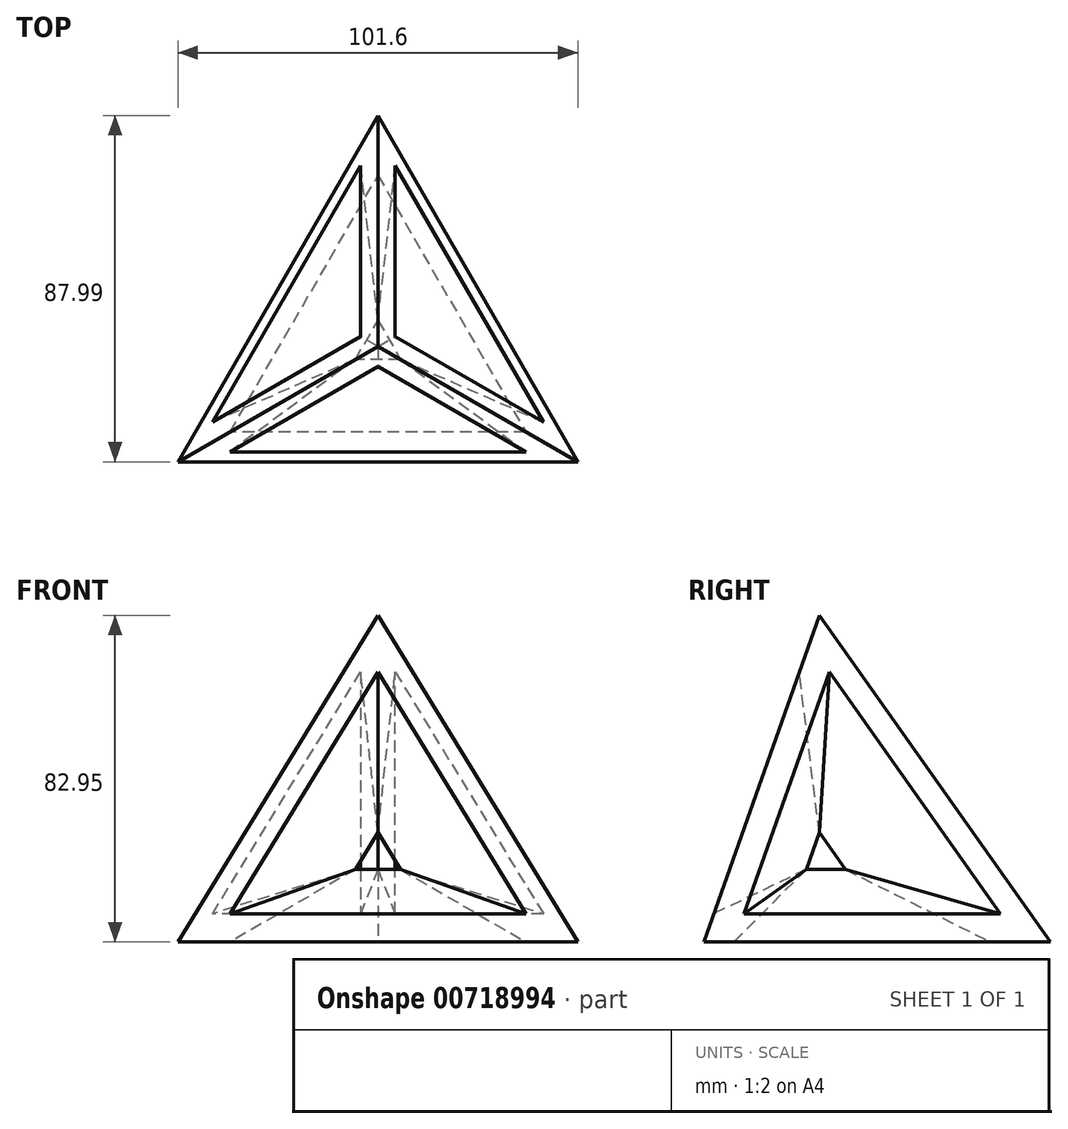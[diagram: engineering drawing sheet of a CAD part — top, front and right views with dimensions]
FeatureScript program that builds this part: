
annotation { "Feature Type Name" : "Feature", "Feature Type Description" : "" }
export const myFeature = defineFeature(function(context is Context, id is Id, definition is map)
    precondition{}
    {
        {
            var Q0;
            Q0=qCreatedBy(makeId("Top.planeOp"),FACE);
            var sketch = newSketch(context, id + "F0", { "sketchPlane" : qUnion([Q0])});
            skLineSegment(sketch, "E0", {"start": v(0, 87.99) * mm, "end": v(-50.8, 0) * mm});
            skLineSegment(sketch, "E1", {"start": v(-50.8, 0) * mm, "end": v(50.8, 0) * mm});
            skLineSegment(sketch, "E2", {"start": v(50.8, 0) * mm, "end": v(0, 87.99) * mm});
            skSolve(sketch);
        }
        {
            var Q0;
            Q0 = qSketchRegion(id + "F0", true);
            extrude(context, id + "F1", {"entities" : qUnion([Q0]), "depth" : 101.6 * mm, "offsetDistance" : 25.4 * mm, "hasDraft" : true, "draftAngle" : 19.47 * degree, "draftPullDirection" : true});
        }
        {
            var Q0;
            Q0=makeQuery(id+"F1.opExtrude","SWEPT_FACE",FACE,{"disambiguationData":[OSD([sQuery(id+"F0.wireOp",EDGE,"E1")])]});
            var sketch = newSketch(context, id + "F2", { "sketchPlane" : qUnion([Q0])});
            skLineSegment(sketch, "E3", {"start": v(0, 72.75) * mm, "end": v(-37.6, 7.62) * mm});
            skLineSegment(sketch, "E4", {"start": v(-37.6, 7.62) * mm, "end": v(37.6, 7.62) * mm});
            skLineSegment(sketch, "E5", {"start": v(37.6, 7.62) * mm, "end": v(0, 72.75) * mm});
            skSolve(sketch);
        }
        {
            var Q0;
            Q0 = qSketchRegion(id + "F2", true);
            extrude(context, id + "F3", {"entities" : qUnion([Q0]), "operationType" : NewBodyOperationType.REMOVE, "oppositeDirection" : true, "depth" : 25.4 * mm, "offsetDistance" : 25.4 * mm, "hasDraft" : true, "draftAngle" : 45 * degree, "draftPullDirection" : true});
        }
        {
            var Q0;
            Q0=makeQuery(id+"F1.opExtrude","SWEPT_FACE",FACE,{"disambiguationData":[OSD([sQuery(id+"F0.wireOp",EDGE,"E2")])]});
            var sketch = newSketch(context, id + "F4", { "sketchPlane" : qUnion([Q0])});
            skLineSegment(sketch, "E6", {"start": v(13.97, 61.83) * mm, "end": v(-10.65, -9.22) * mm});
            skLineSegment(sketch, "E7", {"start": v(-10.65, -9.22) * mm, "end": v(63.2, 4.99) * mm});
            skLineSegment(sketch, "E8", {"start": v(63.2, 4.99) * mm, "end": v(13.97, 61.83) * mm});
            skSolve(sketch);
        }
        {
            var Q0;
            Q0 = qSketchRegion(id + "F4", true);
            extrude(context, id + "F5", {"entities" : qUnion([Q0]), "operationType" : NewBodyOperationType.REMOVE, "oppositeDirection" : true, "depth" : 25.4 * mm, "offsetDistance" : 25.4 * mm, "hasDraft" : true, "draftAngle" : 45 * degree, "draftPullDirection" : true});
        }
        {
            var Q0;
            Q0=makeQuery(id+"F1.opExtrude","SWEPT_FACE",FACE,{"disambiguationData":[OSD([sQuery(id+"F0.wireOp",EDGE,"E0")])]});
            var sketch = newSketch(context, id + "F6", { "sketchPlane" : qUnion([Q0])});
            skLineSegment(sketch, "E9", {"start": v(-13.97, 61.83) * mm, "end": v(-63.2, 4.99) * mm});
            skLineSegment(sketch, "E10", {"start": v(-63.2, 4.99) * mm, "end": v(10.65, -9.22) * mm});
            skLineSegment(sketch, "E11", {"start": v(10.65, -9.22) * mm, "end": v(-13.97, 61.83) * mm});
            skSolve(sketch);
        }
        {
            var Q0;
            Q0 = qSketchRegion(id + "F6", true);
            extrude(context, id + "F7", {"entities" : qUnion([Q0]), "operationType" : NewBodyOperationType.REMOVE, "oppositeDirection" : true, "depth" : 25.4 * mm, "offsetDistance" : 25.4 * mm, "hasDraft" : true, "draftAngle" : 45 * degree, "draftPullDirection" : true});
        }
        {
            var Q0;
            Q0=makeQuery(id+"F1.opExtrude","CAP_FACE",FACE,{"disambiguationData":[OSD([sQuery(id+"F0.wireOp",EDGE,"E0"),sQuery(id+"F0.wireOp",EDGE,"E1"),sQuery(id+"F0.wireOp",EDGE,"E2")])],"isStart":true});
            var sketch = newSketch(context, id + "F8", { "sketchPlane" : qUnion([Q0])});
            skLineSegment(sketch, "E12", {"start": v(-37.6, -7.62) * mm, "end": v(0, -72.75) * mm});
            skLineSegment(sketch, "E13", {"start": v(0, -72.75) * mm, "end": v(37.6, -7.62) * mm});
            skLineSegment(sketch, "E14", {"start": v(37.6, -7.62) * mm, "end": v(-37.6, -7.62) * mm});
            skSolve(sketch);
        }
        {
            var Q0;
            Q0 = qSketchRegion(id + "F8", true);
            extrude(context, id + "F9", {"entities" : qUnion([Q0]), "operationType" : NewBodyOperationType.REMOVE, "oppositeDirection" : true, "depth" : 25.4 * mm, "offsetDistance" : 25.4 * mm, "hasDraft" : true, "draftAngle" : 45 * degree, "draftPullDirection" : true});
        }
    });
